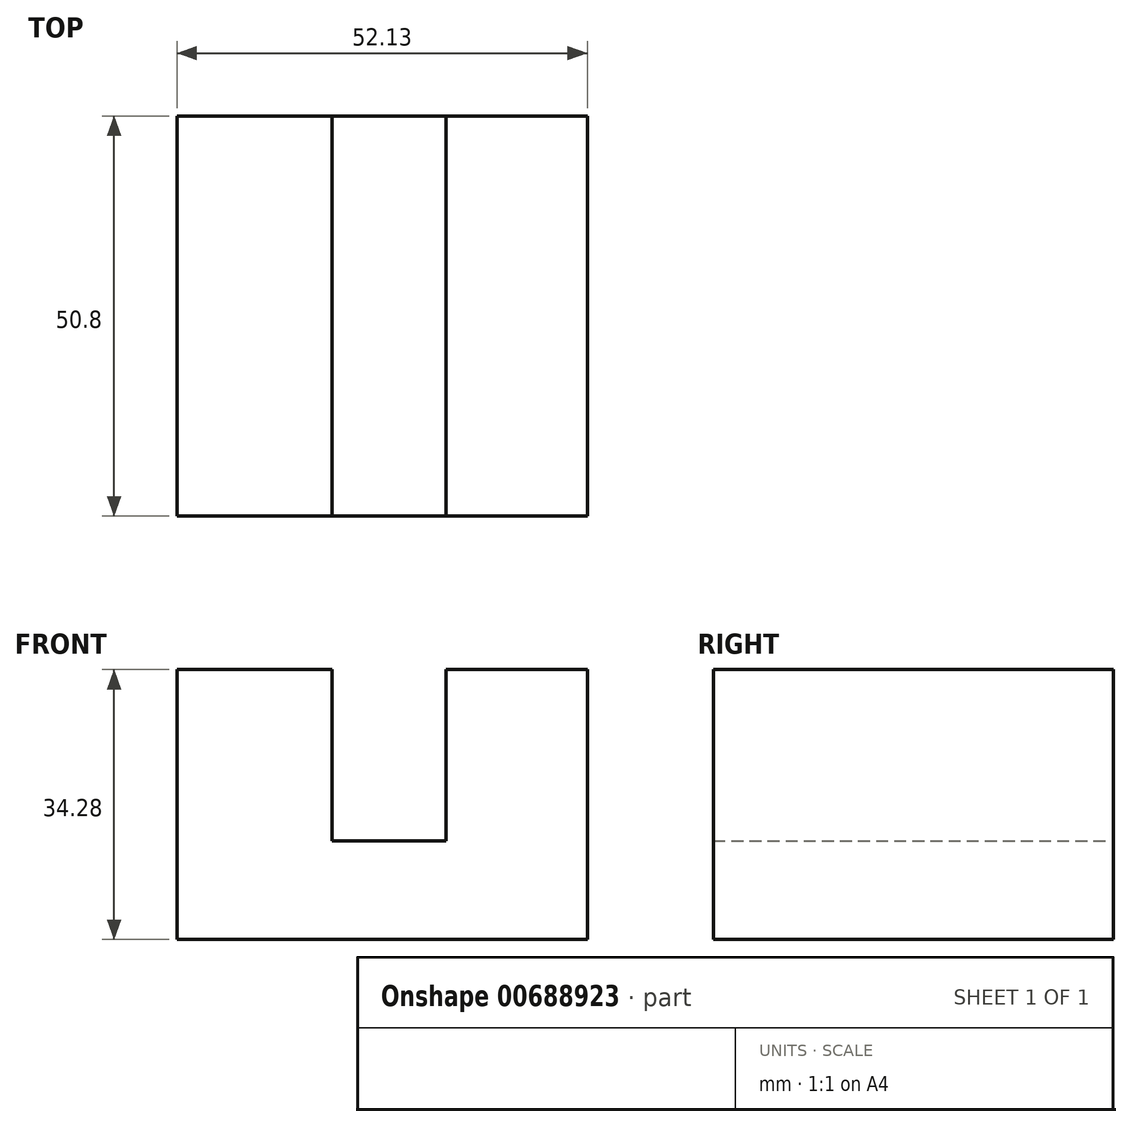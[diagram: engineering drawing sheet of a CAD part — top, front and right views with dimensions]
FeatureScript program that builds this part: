
annotation { "Feature Type Name" : "Feature", "Feature Type Description" : "" }
export const myFeature = defineFeature(function(context is Context, id is Id, definition is map)
    precondition{}
    {
        {
            var Q0;
            Q0=qCreatedBy(makeId("Front.planeOp"),FACE);
            var sketch = newSketch(context, id + "F0", { "sketchPlane" : qUnion([Q0])});
            skLineSegment(sketch, "E0", {"start": v(-24.54, 0) * mm, "end": v(27.6, 0) * mm});
            skLineSegment(sketch, "E1", {"start": v(27.6, 0) * mm, "end": v(27.6, 34.28) * mm});
            skLineSegment(sketch, "E2", {"start": v(27.6, 34.28) * mm, "end": v(9.64, 34.28) * mm});
            skLineSegment(sketch, "E3", {"start": v(9.64, 34.28) * mm, "end": v(9.64, 12.5) * mm});
            skLineSegment(sketch, "E4", {"start": v(9.64, 12.5) * mm, "end": v(-4.87, 12.5) * mm});
            skLineSegment(sketch, "E5", {"start": v(-4.87, 12.5) * mm, "end": v(-4.87, 34.28) * mm});
            skLineSegment(sketch, "E6", {"start": v(-4.87, 34.28) * mm, "end": v(-24.54, 34.28) * mm});
            skLineSegment(sketch, "E7", {"start": v(-24.54, 34.28) * mm, "end": v(-24.54, 0) * mm});
            skSolve(sketch);
        }
        {
            var Q0;
            Q0 = qSketchRegion(id + "F0", true);
            extrude(context, id + "F1", {"entities" : qUnion([Q0]), "depth" : 50.8 * mm, "offsetDistance" : 25.4 * mm});
        }
    });
